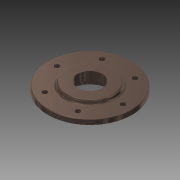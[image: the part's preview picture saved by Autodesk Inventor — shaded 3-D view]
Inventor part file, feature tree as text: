
AUTODESK INVENTOR PART (.ipt)
format: ipt  version: 2015 (Build 190159000, 159)  size: 161,792 bytes
history: native  units: mm
features: extrude x6, sketch x6, fillet x2, pattern_circular x1
ambient origin geometry x8: Origin, YZ Plane, XZ Plane, XY Plane, X Axis, Y Axis, Z Axis, Center Point
bodies: 实体1 (feature_tree)
feature tree (15):
  extrude  "拉伸1"  Depth=8.0mm TaperAngle=0.0deg
  extrude  "拉伸2"  Depth=60.0mm
  extrude  "拉伸3"  Depth=12.0mm
  fillet  "圆角2"  Radius=78.0mm
  extrude  "拉伸5"  Depth=1.0mm
  pattern_circular  "环形阵列1"  [2 undecoded]
  extrude  "拉伸6"  Depth=1.0mm TaperAngle=0.0deg
  extrude  "拉伸7"  Depth=3.0mm TaperAngle=360.0deg
  fillet  "圆角3"  Radius=80.0mm
  sketch  "草图1"  dims[d0=140.0mm d1=8.0mm d2=0.0mm]
  sketch  "草图2"  dims[d3=80.0mm d4=60.0mm]
  sketch  "草图3"  dims[d5=12.0mm d6=0.0mm d7=80.0mm d8=78.0mm]
  sketch  "草图5"  dims[d9=4.0mm d10=0.0mm d15=1.0mm]
  sketch  "草图6"  dims[d16=8.0mm]
  sketch  "草图7"  dims[d17=8.161024mm d18=55.0mm d19=1.0mm d20=0.0mm d21=60.0mm d22=360.0deg d24=80.0mm d25=6.0mm d26=0.0mm d27=41.0mm d28=6.0mm d29=0.0mm d30=3.0mm]
note: 2 required parameter values undecoded (feature->parameter linkage not recoverable at this tier; creation-order binding heuristic only, values carry confidence <= 0.55)
